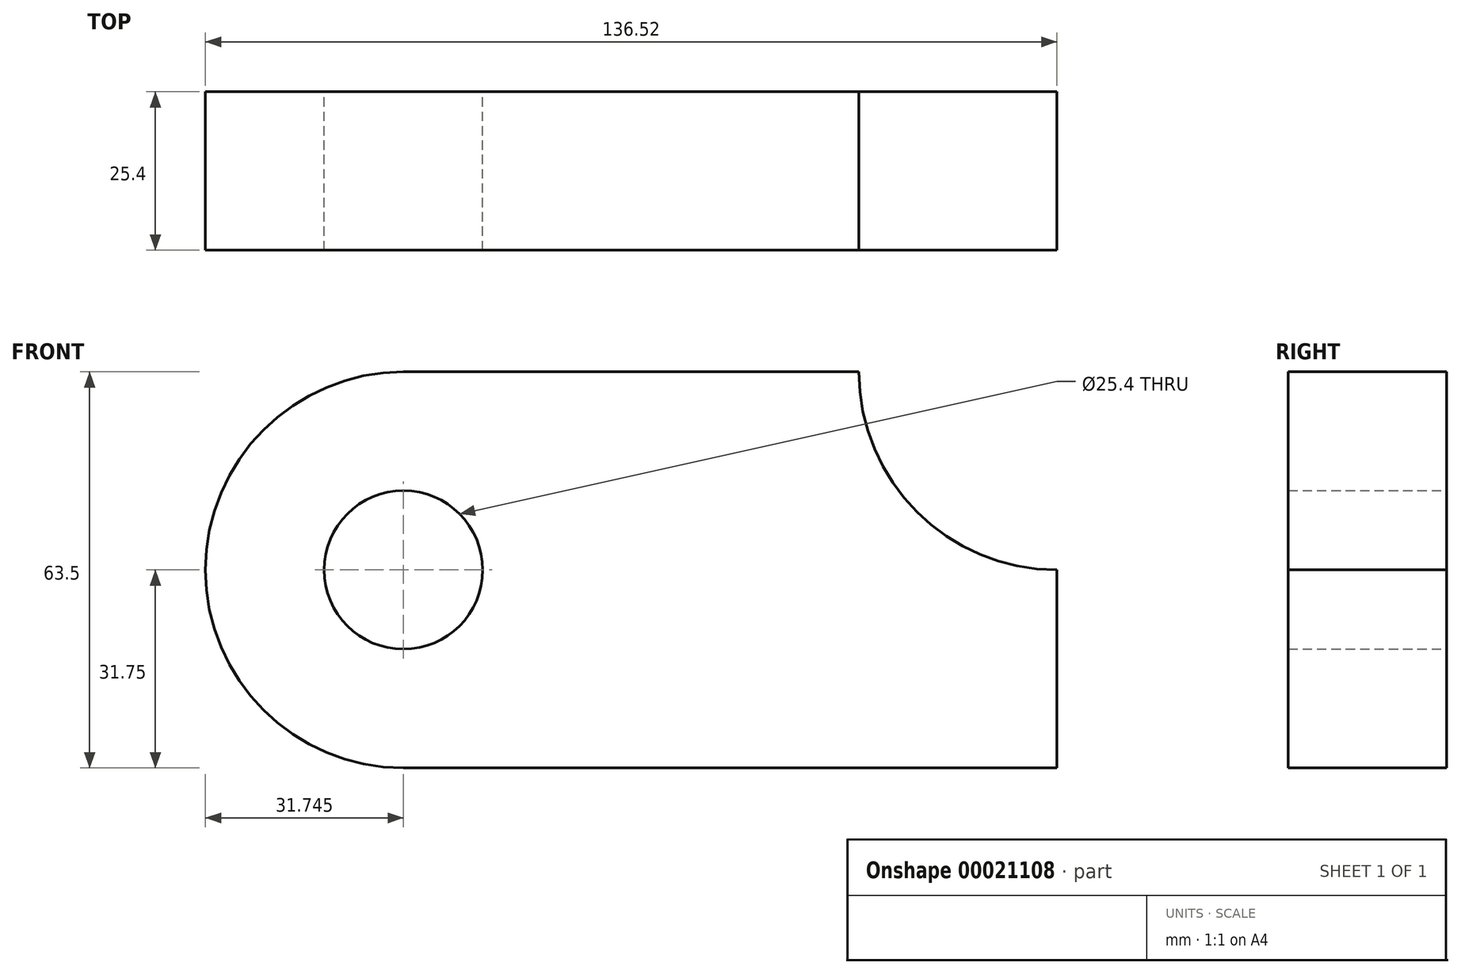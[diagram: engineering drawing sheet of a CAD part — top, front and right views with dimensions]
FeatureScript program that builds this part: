
annotation { "Feature Type Name" : "Feature", "Feature Type Description" : "" }
export const myFeature = defineFeature(function(context is Context, id is Id, definition is map)
    precondition{}
    {
        {
            var Q0;
            Q0=qCreatedBy(makeId("Front.planeOp"),FACE);
            var sketch = newSketch(context, id + "F0", { "sketchPlane" : qUnion([Q0])});
            skLineSegment(sketch, "E0.bottom", {"start": v(-104.78, 63.5) * mm, "end": v(0, 63.5) * mm});
            skLineSegment(sketch, "E0.top", {"start": v(-104.78, 0) * mm, "end": v(0, 0) * mm});
            skLineSegment(sketch, "E0.left", {"start": v(-104.78, 63.5) * mm, "end": v(-104.78, 0) * mm});
            skLineSegment(sketch, "E0.right", {"start": v(0, 63.5) * mm, "end": v(0, 0) * mm});
            skCircle(sketch, "E1", {"center": v(-104.78, 31.75) * mm, "radius": 31.75 * mm});
            skLineSegment(sketch, "E2", {"start": v(0, 63.5) * mm, "end": v(0, 31.75) * mm});
            skCircle(sketch, "E3", {"center": v(0, 63.5) * mm, "radius": 31.75 * mm});
            skCircle(sketch, "E4", {"center": v(-104.78, 31.75) * mm, "radius": 12.7 * mm});
            skSolve(sketch);
        }
        {
            var Q0;
            {var subQ5=sQuery(id+"F0.wireOp",EDGE,"E0.top");Q0=makeQuery(id+"F0.imprint","IMPRINT",FACE,{"disambiguationData":[TD([[makeQuery(id+"F0.imprint","IMPRINT",EDGE,{"derivedFrom":subQ5}),1.0]])]});}
            var Q1;
            {var subQ1=sQuery(id+"F0.wireOp",EDGE,"E0.left");var subQ4=sQuery(id+"F0.wireOp",EDGE,"E4");var subQ6=makeQuery(id+"F0.imprint","INTERSECT",VERTEX,{"disambiguationData":[OD(0.0)],"derivedFrom":[subQ1,subQ4]});Q1=makeQuery(id+"F0.imprint","IMPRINT",FACE,{"disambiguationData":[TD([[makeQuery(id+"F0.imprint","IMPRINT",EDGE,{"disambiguationData":[TD([[subQ6,-1.0]])],"derivedFrom":subQ4}),-1.0]])]});}
            var Q2;
            {var subQ0=sQuery(id+"F0.wireOp",EDGE,"E4");var subQ1=sQuery(id+"F0.wireOp",EDGE,"E0.left");var subQ3=makeQuery(id+"F0.imprint","INTERSECT",VERTEX,{"disambiguationData":[OD(0.0)],"derivedFrom":[subQ1,subQ0]});Q2=makeQuery(id+"F0.imprint","IMPRINT",FACE,{"disambiguationData":[TD([[makeQuery(id+"F0.imprint","IMPRINT",EDGE,{"disambiguationData":[TD([[subQ3,1.0]])],"derivedFrom":subQ0}),-1.0]])]});}
            extrude(context, id + "F1", {"entities" : qUnion([Q0, Q1, Q2]), "depth" : 25.4 * mm});
        }
    });
